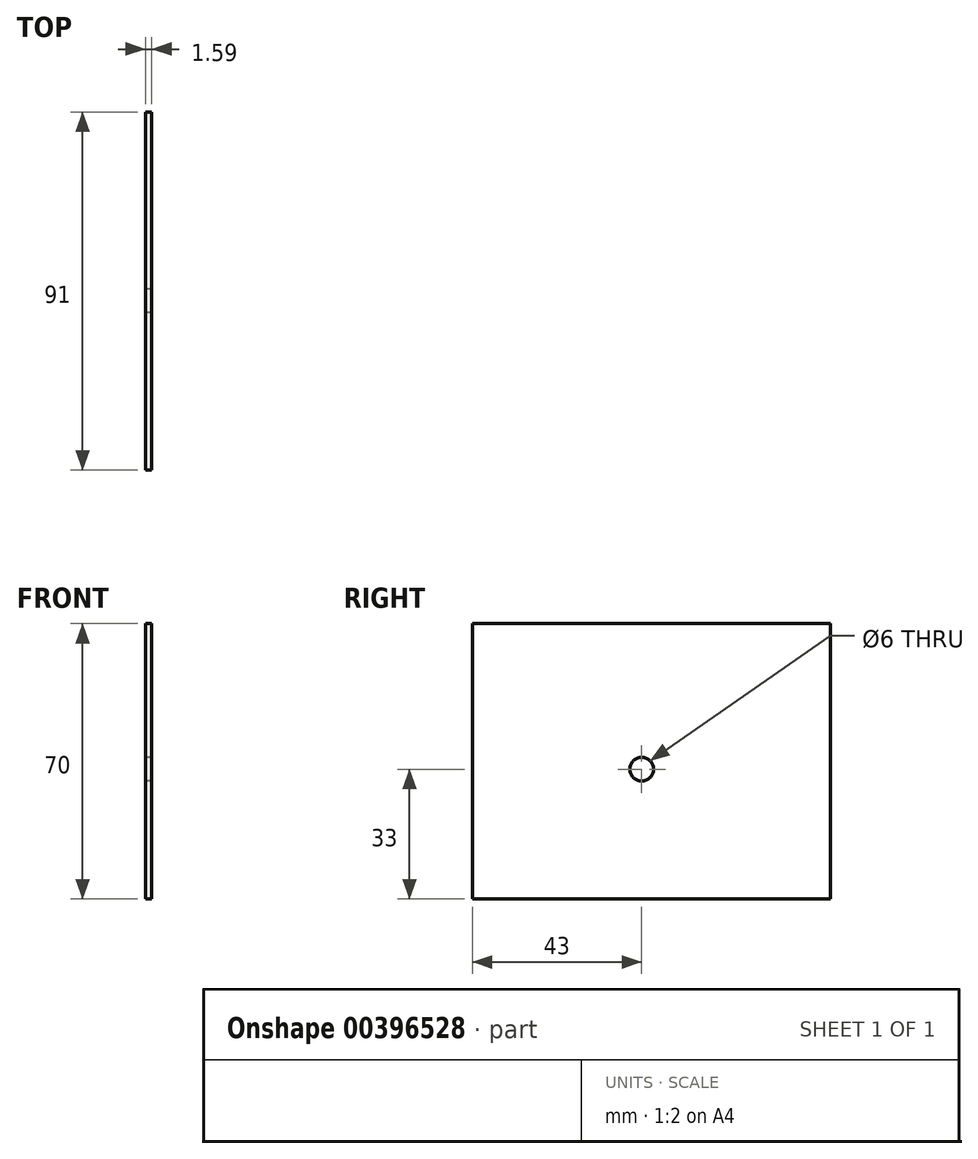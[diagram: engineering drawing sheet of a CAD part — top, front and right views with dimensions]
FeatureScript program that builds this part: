
annotation { "Feature Type Name" : "Feature", "Feature Type Description" : "" }
export const myFeature = defineFeature(function(context is Context, id is Id, definition is map)
    precondition{}
    {
        {
            var Q0;
            Q0=qCreatedBy(makeId("Right.planeOp"),FACE);
            var sketch = newSketch(context, id + "F0", { "sketchPlane" : qUnion([Q0])});
            skLineSegment(sketch, "E0.bottom", {"start": v(45.5, -35) * mm, "end": v(-45.5, -35) * mm});
            skLineSegment(sketch, "E0.top", {"start": v(45.5, 35) * mm, "end": v(-45.5, 35) * mm});
            skLineSegment(sketch, "E0.left", {"start": v(45.5, -35) * mm, "end": v(45.5, 35) * mm});
            skLineSegment(sketch, "E0.right", {"start": v(-45.5, -35) * mm, "end": v(-45.5, 35) * mm});
            skPoint(sketch, "E0.middle", {"position": v(0, 0) * mm});
            skCircle(sketch, "E1", {"center": v(-2.5, -2) * mm, "radius": 3 * mm});
            skSolve(sketch);
        }
        {
            var Q0;
            Q0=makeQuery(id+"F0.imprint","IMPRINT",FACE,{"disambiguationData":[TD([[makeQuery(id+"F0.imprint","IMPRINT",EDGE,{"derivedFrom":sQuery(id+"F0.wireOp",EDGE,"E0.bottom")}),-1.0]])]});
            extrude(context, id + "F1", {"entities" : qUnion([Q0]), "depth" : 1.59 * mm});
        }
    });
